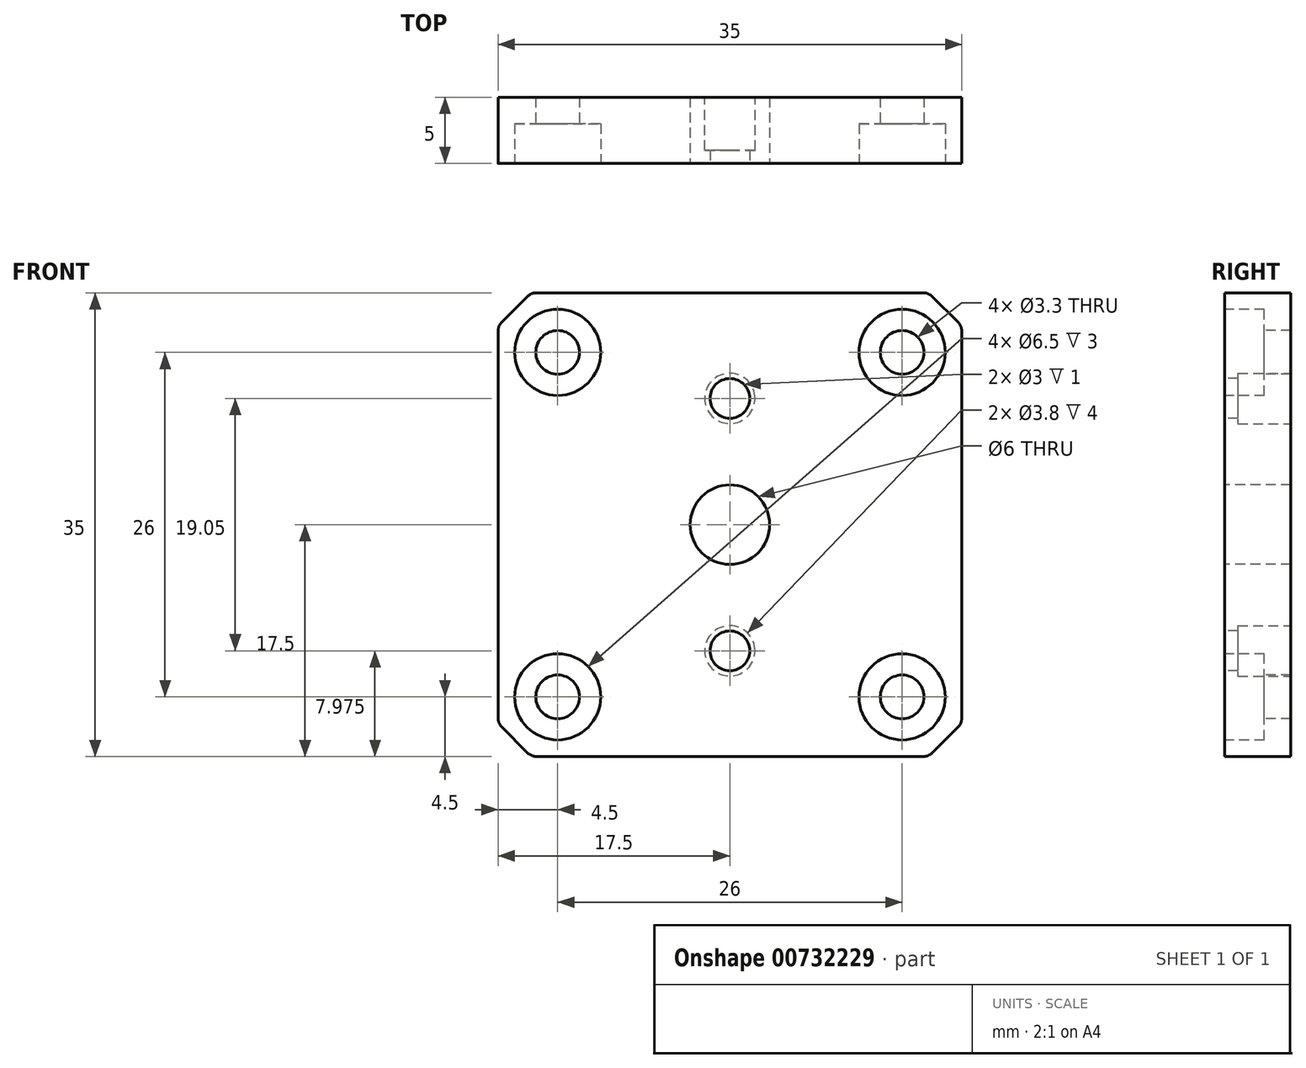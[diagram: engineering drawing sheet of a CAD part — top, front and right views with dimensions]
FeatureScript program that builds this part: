
annotation { "Feature Type Name" : "Feature", "Feature Type Description" : "" }
export const myFeature = defineFeature(function(context is Context, id is Id, definition is map)
    precondition{}
    {
        {
            var Q0;
            Q0=qCreatedBy(makeId("Front.planeOp"),FACE);
            var sketch = newSketch(context, id + "F0", { "sketchPlane" : qUnion([Q0])});
            skLineSegment(sketch, "E0.bottom", {"start": v(-17.5, 17.5) * mm, "end": v(17.5, 17.5) * mm});
            skLineSegment(sketch, "E0.top", {"start": v(-17.5, -17.5) * mm, "end": v(17.5, -17.5) * mm});
            skLineSegment(sketch, "E0.left", {"start": v(-17.5, 17.5) * mm, "end": v(-17.5, -17.5) * mm});
            skLineSegment(sketch, "E0.right", {"start": v(17.5, 17.5) * mm, "end": v(17.5, -17.5) * mm});
            skPoint(sketch, "E0.middle", {"position": v(0, 0) * mm});
            skSolve(sketch);
        }
        {
            var Q0;
            Q0 = qSketchRegion(id + "F0", true);
            extrude(context, id + "F1", {"entities" : qUnion([Q0]), "depth" : 5 * mm, "offsetDistance" : 25 * mm});
        }
        {
            var Q0;
            Q0=makeQuery(id+"F1.opExtrude","CAP_FACE",FACE,{"disambiguationData":[OSD([sQuery(id+"F0.wireOp",EDGE,"E0.bottom"),sQuery(id+"F0.wireOp",EDGE,"E0.top"),sQuery(id+"F0.wireOp",EDGE,"E0.left"),sQuery(id+"F0.wireOp",EDGE,"E0.right")])],"isStart":false});
            var sketch = newSketch(context, id + "F2", { "sketchPlane" : qUnion([Q0])});
            skLineSegment(sketch, "E1", {"start": v(0, 17.5) * mm, "end": v(0, -17.5) * mm, "construction": true});
            skCircle(sketch, "E2", {"center": v(0, 0) * mm, "radius": 3 * mm});
            skSolve(sketch);
        }
        {
            var Q0;
            Q0 = qSketchRegion(id + "F2", true);
            extrude(context, id + "F3", {"entities" : qUnion([Q0]), "operationType" : NewBodyOperationType.REMOVE, "endBound" : BoundingType.THROUGH_ALL, "oppositeDirection" : true, "depth" : 25 * mm, "offsetDistance" : 25 * mm});
        }
        {
            var Q0;
            Q0=makeQuery(id+"F1.opExtrude","CAP_FACE",FACE,{"disambiguationData":[OSD([sQuery(id+"F0.wireOp",EDGE,"E0.bottom"),sQuery(id+"F0.wireOp",EDGE,"E0.top"),sQuery(id+"F0.wireOp",EDGE,"E0.left"),sQuery(id+"F0.wireOp",EDGE,"E0.right")])],"isStart":false});
            var sketch = newSketch(context, id + "F4", { "sketchPlane" : qUnion([Q0])});
            skPoint(sketch, "E3", {"position": v(-13, 13) * mm});
            skLineSegment(sketch, "E4", {"start": v(0, 17.5) * mm, "end": v(0, -17.5) * mm, "construction": true});
            skPoint(sketch, "E5", {"position": v(0, 0) * mm});
            skPoint(sketch, "E6.1.0", {"position": v(-13, -13) * mm});
            skPoint(sketch, "E6.2.0", {"position": v(13, -13) * mm});
            skPoint(sketch, "E6.3.0", {"position": v(13, 13) * mm});
            skSolve(sketch);
        }
        {
            var Q0;
            Q0=sQuery(id+"F4.wireOp",VERTEX,"E3");
            var Q1;
            Q1=sQuery(id+"F4.wireOp",VERTEX,"E6.3.0");
            var Q2;
            Q2=sQuery(id+"F4.wireOp",VERTEX,"E6.2.0");
            var Q3;
            Q3=sQuery(id+"F4.wireOp",VERTEX,"E6.1.0");
            var Q4;
            Q4=makeQuery(id+"F1.opExtrude","SWEPT_BODY",BODY,{"disambiguationData":[OSD([sQuery(id+"F0.wireOp",EDGE,"E0.bottom"),sQuery(id+"F0.wireOp",EDGE,"E0.top"),sQuery(id+"F0.wireOp",EDGE,"E0.left"),sQuery(id+"F0.wireOp",EDGE,"E0.right")])]});
            hole(context, id + "F5", {"style" : HoleStyle.C_BORE, "endStyle" : HoleEndStyle.THROUGH, "standardTappedOrClearance" : lookupTablePath({ "standard" : "ISO", "fit" : "Normal", "size" : "M3", "type" : "Clearance" }), "standardBlindInLast" : lookupTablePath({ "fit" : "Standard", "standard" : "ISO", "size" : "M3", "type" : "Clearance" }), "holeDiameter" : 3.3 * mm, "cBoreDiameter" : 6.5 * mm, "cBoreDepth" : 3 * mm, "majorDiameter" : 5 * mm, "isTappedThrough" : true, "tappedDepth" : 12 * mm, "tapClearance" : 3, "locations" : qUnion([Q0, Q1, Q2, Q3]), "scope" : qUnion([Q4])});
        }
        {
            var Q0;
            Q0=makeQuery(id+"F1.opExtrude","SWEPT_EDGE",EDGE,{"disambiguationData":[OSD([sQuery(id+"F0.wireOp",EDGE,"E0.bottom"),sQuery(id+"F0.wireOp",EDGE,"E0.right")])]});
            var Q1;
            Q1=makeQuery(id+"F1.opExtrude","SWEPT_EDGE",EDGE,{"disambiguationData":[OSD([sQuery(id+"F0.wireOp",EDGE,"E0.bottom"),sQuery(id+"F0.wireOp",EDGE,"E0.left")])]});
            var Q2;
            Q2=makeQuery(id+"F1.opExtrude","SWEPT_EDGE",EDGE,{"disambiguationData":[OSD([sQuery(id+"F0.wireOp",EDGE,"E0.top"),sQuery(id+"F0.wireOp",EDGE,"E0.right")])]});
            var Q3;
            Q3=makeQuery(id+"F1.opExtrude","SWEPT_EDGE",EDGE,{"disambiguationData":[OSD([sQuery(id+"F0.wireOp",EDGE,"E0.top"),sQuery(id+"F0.wireOp",EDGE,"E0.left")])]});
            chamfer(context, id + "F6", {"entities" : qUnion([Q0, Q1, Q2, Q3]), "width" : 2.5 * mm, "tangentPropagation" : true});
        }
        {
            var Q0;
            {var subQ0=sQuery(id+"F0.wireOp",EDGE,"E0.bottom");Q0=makeQuery(id+"F6.opChamfer","BLEND_EDGE",EDGE,{"blendedFrom":[makeQuery(id+"F1.opExtrude","SWEPT_EDGE",EDGE,{"disambiguationData":[OSD([subQ0,sQuery(id+"F0.wireOp",EDGE,"E0.right")])]}),makeQuery(id+"F1.opExtrude","SWEPT_FACE",FACE,{"disambiguationData":[OSD([subQ0])]})],"blendedInto":[makeQuery(id+"F1.opExtrude","SWEPT_FACE",FACE,{"disambiguationData":[OSD([subQ0])]})]});}
            var Q1;
            {var subQ0=sQuery(id+"F0.wireOp",EDGE,"E0.right");Q1=makeQuery(id+"F6.opChamfer","BLEND_EDGE",EDGE,{"blendedFrom":[makeQuery(id+"F1.opExtrude","SWEPT_EDGE",EDGE,{"disambiguationData":[OSD([sQuery(id+"F0.wireOp",EDGE,"E0.bottom"),subQ0])]}),makeQuery(id+"F1.opExtrude","SWEPT_FACE",FACE,{"disambiguationData":[OSD([subQ0])]})],"blendedInto":[makeQuery(id+"F1.opExtrude","SWEPT_FACE",FACE,{"disambiguationData":[OSD([subQ0])]})]});}
            var Q2;
            {var subQ0=sQuery(id+"F0.wireOp",EDGE,"E0.right");Q2=makeQuery(id+"F6.opChamfer","BLEND_EDGE",EDGE,{"blendedFrom":[makeQuery(id+"F1.opExtrude","SWEPT_EDGE",EDGE,{"disambiguationData":[OSD([sQuery(id+"F0.wireOp",EDGE,"E0.top"),subQ0])]}),makeQuery(id+"F1.opExtrude","SWEPT_FACE",FACE,{"disambiguationData":[OSD([subQ0])]})],"blendedInto":[makeQuery(id+"F1.opExtrude","SWEPT_FACE",FACE,{"disambiguationData":[OSD([subQ0])]})]});}
            var Q3;
            {var subQ0=sQuery(id+"F0.wireOp",EDGE,"E0.top");Q3=makeQuery(id+"F6.opChamfer","BLEND_EDGE",EDGE,{"blendedFrom":[makeQuery(id+"F1.opExtrude","SWEPT_EDGE",EDGE,{"disambiguationData":[OSD([subQ0,sQuery(id+"F0.wireOp",EDGE,"E0.right")])]}),makeQuery(id+"F1.opExtrude","SWEPT_FACE",FACE,{"disambiguationData":[OSD([subQ0])]})],"blendedInto":[makeQuery(id+"F1.opExtrude","SWEPT_FACE",FACE,{"disambiguationData":[OSD([subQ0])]})]});}
            var Q4;
            {var subQ0=sQuery(id+"F0.wireOp",EDGE,"E0.top");Q4=makeQuery(id+"F6.opChamfer","BLEND_EDGE",EDGE,{"blendedFrom":[makeQuery(id+"F1.opExtrude","SWEPT_EDGE",EDGE,{"disambiguationData":[OSD([subQ0,sQuery(id+"F0.wireOp",EDGE,"E0.left")])]}),makeQuery(id+"F1.opExtrude","SWEPT_FACE",FACE,{"disambiguationData":[OSD([subQ0])]})],"blendedInto":[makeQuery(id+"F1.opExtrude","SWEPT_FACE",FACE,{"disambiguationData":[OSD([subQ0])]})]});}
            var Q5;
            {var subQ0=sQuery(id+"F0.wireOp",EDGE,"E0.left");Q5=makeQuery(id+"F6.opChamfer","BLEND_EDGE",EDGE,{"blendedFrom":[makeQuery(id+"F1.opExtrude","SWEPT_EDGE",EDGE,{"disambiguationData":[OSD([sQuery(id+"F0.wireOp",EDGE,"E0.top"),subQ0])]}),makeQuery(id+"F1.opExtrude","SWEPT_FACE",FACE,{"disambiguationData":[OSD([subQ0])]})],"blendedInto":[makeQuery(id+"F1.opExtrude","SWEPT_FACE",FACE,{"disambiguationData":[OSD([subQ0])]})]});}
            var Q6;
            {var subQ0=sQuery(id+"F0.wireOp",EDGE,"E0.bottom");Q6=makeQuery(id+"F6.opChamfer","BLEND_EDGE",EDGE,{"blendedFrom":[makeQuery(id+"F1.opExtrude","SWEPT_EDGE",EDGE,{"disambiguationData":[OSD([subQ0,sQuery(id+"F0.wireOp",EDGE,"E0.left")])]}),makeQuery(id+"F1.opExtrude","SWEPT_FACE",FACE,{"disambiguationData":[OSD([subQ0])]})],"blendedInto":[makeQuery(id+"F1.opExtrude","SWEPT_FACE",FACE,{"disambiguationData":[OSD([subQ0])]})]});}
            var Q7;
            {var subQ0=sQuery(id+"F0.wireOp",EDGE,"E0.left");Q7=makeQuery(id+"F6.opChamfer","BLEND_EDGE",EDGE,{"blendedFrom":[makeQuery(id+"F1.opExtrude","SWEPT_EDGE",EDGE,{"disambiguationData":[OSD([sQuery(id+"F0.wireOp",EDGE,"E0.bottom"),subQ0])]}),makeQuery(id+"F1.opExtrude","SWEPT_FACE",FACE,{"disambiguationData":[OSD([subQ0])]})],"blendedInto":[makeQuery(id+"F1.opExtrude","SWEPT_FACE",FACE,{"disambiguationData":[OSD([subQ0])]})]});}
            fillet(context, id + "F7", {"entities" : qUnion([Q0, Q1, Q2, Q3, Q4, Q5, Q6, Q7]), "radius" : 1 * mm, "tangentPropagation" : true, "allowEdgeOverflow" : false});
        }
        {
            var Q0;
            Q0=makeQuery(id+"F1.opExtrude","CAP_FACE",FACE,{"disambiguationData":[OSD([sQuery(id+"F0.wireOp",EDGE,"E0.bottom"),sQuery(id+"F0.wireOp",EDGE,"E0.top"),sQuery(id+"F0.wireOp",EDGE,"E0.left"),sQuery(id+"F0.wireOp",EDGE,"E0.right")])],"isStart":false});
            var sketch = newSketch(context, id + "F8", { "sketchPlane" : qUnion([Q0])});
            skLineSegment(sketch, "E7", {"start": v(0, 17.5) * mm, "end": v(0, -17.5) * mm, "construction": true});
            skCircle(sketch, "E8", {"center": v(0, 9.53) * mm, "radius": 1.5 * mm});
            skCircle(sketch, "E9", {"center": v(0, -9.53) * mm, "radius": 1.5 * mm});
            skSolve(sketch);
        }
        {
            var Q0;
            Q0 = qSketchRegion(id + "F8", true);
            extrude(context, id + "F9", {"entities" : qUnion([Q0]), "operationType" : NewBodyOperationType.REMOVE, "endBound" : BoundingType.THROUGH_ALL, "oppositeDirection" : true, "depth" : 25 * mm, "offsetDistance" : 25 * mm});
        }
        {
            var Q0;
            Q0=makeQuery(id+"F1.opExtrude","CAP_FACE",FACE,{"disambiguationData":[OSD([sQuery(id+"F0.wireOp",EDGE,"E0.bottom"),sQuery(id+"F0.wireOp",EDGE,"E0.top"),sQuery(id+"F0.wireOp",EDGE,"E0.left"),sQuery(id+"F0.wireOp",EDGE,"E0.right")])],"isStart":true});
            var sketch = newSketch(context, id + "F10", { "sketchPlane" : qUnion([Q0])});
            skCircle(sketch, "E10", {"center": v(0, -9.53) * mm, "radius": 1.9 * mm});
            skCircle(sketch, "E11", {"center": v(0, 9.53) * mm, "radius": 1.9 * mm});
            skSolve(sketch);
        }
        {
            var Q0;
            Q0 = qSketchRegion(id + "F10", true);
            extrude(context, id + "F11", {"entities" : qUnion([Q0]), "operationType" : NewBodyOperationType.REMOVE, "oppositeDirection" : true, "depth" : 4 * mm, "offsetDistance" : 25 * mm});
        }
    });
